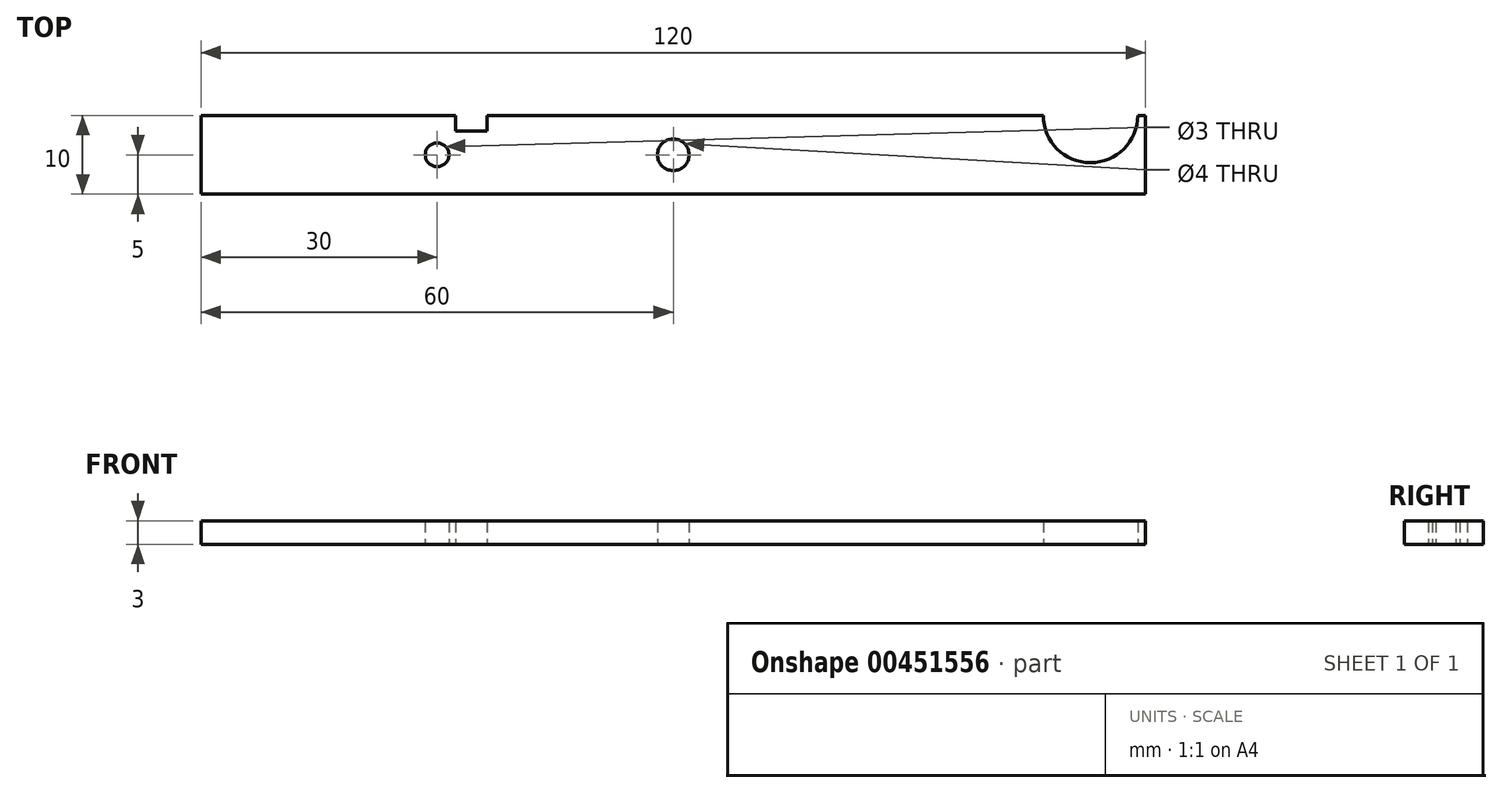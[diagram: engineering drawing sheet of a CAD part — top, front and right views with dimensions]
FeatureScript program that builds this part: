
annotation { "Feature Type Name" : "Feature", "Feature Type Description" : "" }
export const myFeature = defineFeature(function(context is Context, id is Id, definition is map)
    precondition{}
    {
        {
            var Q0;
            Q0=qCreatedBy(makeId("Top.planeOp"),FACE);
            var sketch = newSketch(context, id + "F0", { "sketchPlane" : qUnion([Q0])});
            skLineSegment(sketch, "E0.bottom", {"start": v(-60, 5) * mm, "end": v(60, 5) * mm});
            skLineSegment(sketch, "E0.top", {"start": v(-60, -5) * mm, "end": v(60, -5) * mm});
            skLineSegment(sketch, "E0.left", {"start": v(-60, 5) * mm, "end": v(-60, -5) * mm});
            skLineSegment(sketch, "E0.right", {"start": v(60, 5) * mm, "end": v(60, -5) * mm});
            skPoint(sketch, "E0.middle", {"position": v(0, 0) * mm});
            skLineSegment(sketch, "E1.bottom", {"start": v(-23.68, 5) * mm, "end": v(-27.68, 5) * mm});
            skLineSegment(sketch, "E1.top", {"start": v(-23.68, 3) * mm, "end": v(-27.68, 3) * mm});
            skLineSegment(sketch, "E1.left", {"start": v(-23.68, 5) * mm, "end": v(-23.68, 3) * mm});
            skLineSegment(sketch, "E1.right", {"start": v(-27.68, 5) * mm, "end": v(-27.68, 3) * mm});
            skCircle(sketch, "E2", {"center": v(0, 0) * mm, "radius": 2 * mm});
            skCircle(sketch, "E3", {"center": v(0, 0) * mm, "radius": 7 * mm});
            skCircle(sketch, "E4", {"center": v(-30, 0) * mm, "radius": 1.5 * mm});
            skCircle(sketch, "E5", {"center": v(53, 5) * mm, "radius": 6 * mm});
            skSolve(sketch);
        }
        {
            var Q0;
            {var subQ0=sQuery(id+"F0.wireOp",EDGE,"E0.left");Q0=makeQuery(id+"F0.imprint","IMPRINT",FACE,{"disambiguationData":[TD([[makeQuery(id+"F0.imprint","IMPRINT",EDGE,{"derivedFrom":subQ0}),1.0]])]});}
            var Q1;
            {var subQ0=sQuery(id+"F0.wireOp",EDGE,"E0.right");Q1=makeQuery(id+"F0.imprint","IMPRINT",FACE,{"disambiguationData":[TD([[makeQuery(id+"F0.imprint","IMPRINT",EDGE,{"derivedFrom":subQ0}),-1.0]])]});}
            var Q2;
            Q2=makeQuery(id+"F0.imprint","IMPRINT",FACE,{"disambiguationData":[TD([[makeQuery(id+"F0.imprint","IMPRINT",EDGE,{"derivedFrom":sQuery(id+"F0.wireOp",EDGE,"E2")}),-1.0]])]});
            var Q3;
            {var subQ0=sQuery(id+"F0.wireOp",EDGE,"E3");var subQ1=sQuery(id+"F0.wireOp",EDGE,"E0.top");var subQ2=makeQuery(id+"F0.imprint","INTERSECT",VERTEX,{"disambiguationData":[OD(0.0)],"derivedFrom":[subQ1,subQ0]});Q3=makeQuery(id+"F0.imprint","IMPRINT",FACE,{"disambiguationData":[TD([[makeQuery(id+"F0.imprint","IMPRINT",EDGE,{"disambiguationData":[TD([[subQ2,-1.0]])],"derivedFrom":subQ1}),-1.0]])]});}
            var Q4;
            {var subQ0=sQuery(id+"F0.wireOp",EDGE,"E3");var subQ1=sQuery(id+"F0.wireOp",EDGE,"E0.bottom");var subQ2=makeQuery(id+"F0.imprint","INTERSECT",VERTEX,{"disambiguationData":[OD(0.0)],"derivedFrom":[subQ1,subQ0]});Q4=makeQuery(id+"F0.imprint","IMPRINT",FACE,{"disambiguationData":[TD([[makeQuery(id+"F0.imprint","IMPRINT",EDGE,{"disambiguationData":[TD([[subQ2,-1.0]])],"derivedFrom":subQ1}),1.0]])]});}
            extrude(context, id + "F1", {"entities" : qUnion([Q0, Q1, Q2, Q3, Q4]), "depth" : 3 * mm});
        }
    });
